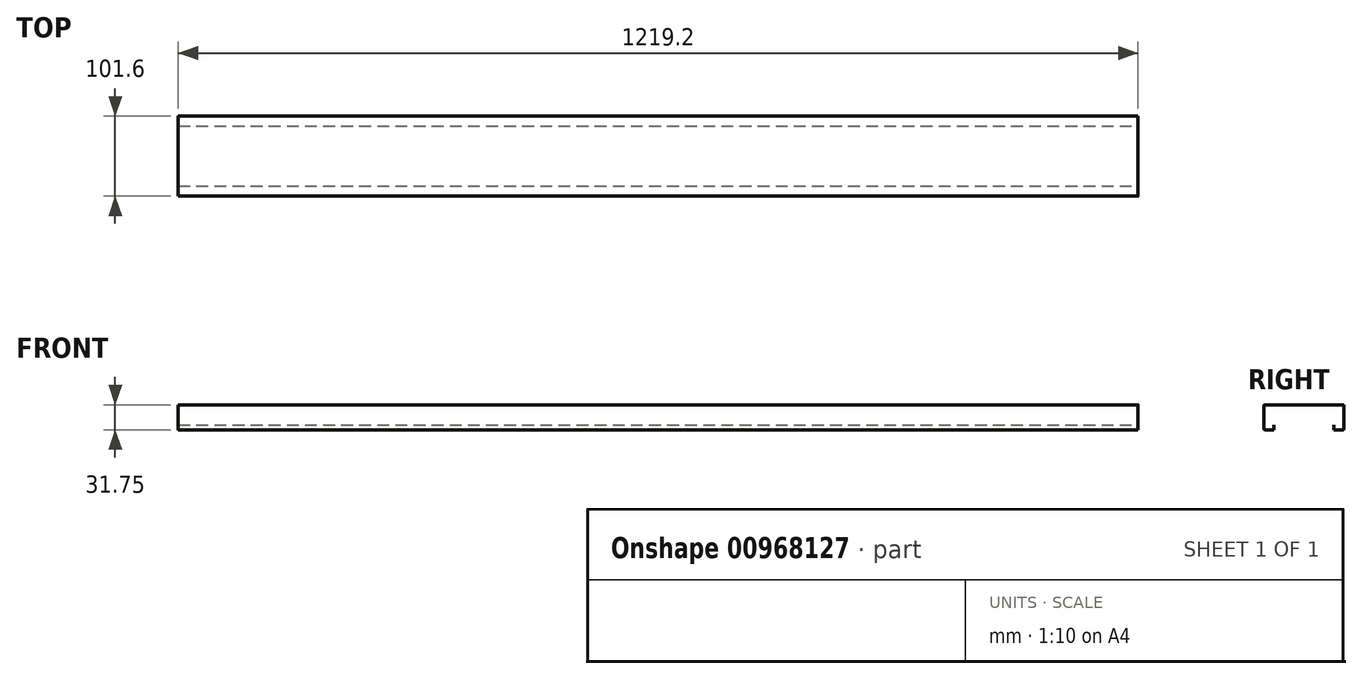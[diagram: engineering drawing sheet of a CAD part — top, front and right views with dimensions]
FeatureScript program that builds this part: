
annotation { "Feature Type Name" : "Feature", "Feature Type Description" : "" }
export const myFeature = defineFeature(function(context is Context, id is Id, definition is map)
    precondition{}
    {
        {
            var Q0;
            Q0=qCreatedBy(makeId("Right.planeOp"),FACE);
            var sketch = newSketch(context, id + "F0", { "sketchPlane" : qUnion([Q0])});
            skLineSegment(sketch, "E0", {"start": v(-50.7, 26.3) * mm, "end": v(50.9, 26.3) * mm});
            skLineSegment(sketch, "E1", {"start": v(-50.7, 26.3) * mm, "end": v(-50.7, -5.44) * mm});
            skLineSegment(sketch, "E2", {"start": v(-50.7, -5.44) * mm, "end": v(-38, -5.44) * mm});
            skLineSegment(sketch, "E3", {"start": v(50.9, 26.3) * mm, "end": v(50.9, -5.44) * mm});
            skLineSegment(sketch, "E4", {"start": v(50.9, -5.44) * mm, "end": v(38.2, -5.44) * mm});
            skLineSegment(sketch, "E5", {"start": v(-38, -5.44) * mm, "end": v(-38, 0.9) * mm});
            skLineSegment(sketch, "E6", {"start": v(38.2, -5.44) * mm, "end": v(38.2, 0.9) * mm});
            skSolve(sketch);
        }
        {
            var Q0;
            Q0=sQuery(id+"F0.wireOp",EDGE,"E0");
            var Q1;
            Q1=sQuery(id+"F0.wireOp",EDGE,"E1");
            var Q2;
            Q2=sQuery(id+"F0.wireOp",EDGE,"E2");
            var Q3;
            Q3=sQuery(id+"F0.wireOp",EDGE,"E5");
            var Q4;
            Q4=sQuery(id+"F0.wireOp",EDGE,"E4");
            var Q5;
            Q5=sQuery(id+"F0.wireOp",EDGE,"E6");
            var Q6;
            Q6=sQuery(id+"F0.wireOp",EDGE,"E3");
            extrude(context, id + "F1", {"bodyType" : ToolBodyType.SURFACE, "surfaceEntities" : qUnion([Q0, Q1, Q2, Q3, Q4, Q5, Q6]), "depth" : 1219.2 * mm, "offsetDistance" : 25.4 * mm});
        }
        {
            var Q0;
            Q0=makeQuery(id+"F1.opExtrude","SWEPT_EDGE",EDGE,{"disambiguationData":[OSD([sQuery(id+"F0.wireOp",VERTEX,"E3.start")])]});
            var Q1;
            Q1=makeQuery(id+"F1.opExtrude","SWEPT_EDGE",EDGE,{"disambiguationData":[OSD([sQuery(id+"F0.wireOp",VERTEX,"E3.end")])]});
            var Q2;
            Q2=makeQuery(id+"F1.opExtrude","SWEPT_EDGE",EDGE,{"disambiguationData":[OSD([sQuery(id+"F0.wireOp",VERTEX,"E2.start")])]});
            var Q3;
            Q3=makeQuery(id+"F1.opExtrude","SWEPT_EDGE",EDGE,{"disambiguationData":[OSD([sQuery(id+"F0.wireOp",VERTEX,"E1.start")])]});
            fillet(context, id + "F2", {"entities" : qUnion([Q0, Q1, Q2, Q3]), "radius" : 1.27 * mm, "tangentPropagation" : true, "allowEdgeOverflow" : false});
        }
    });
